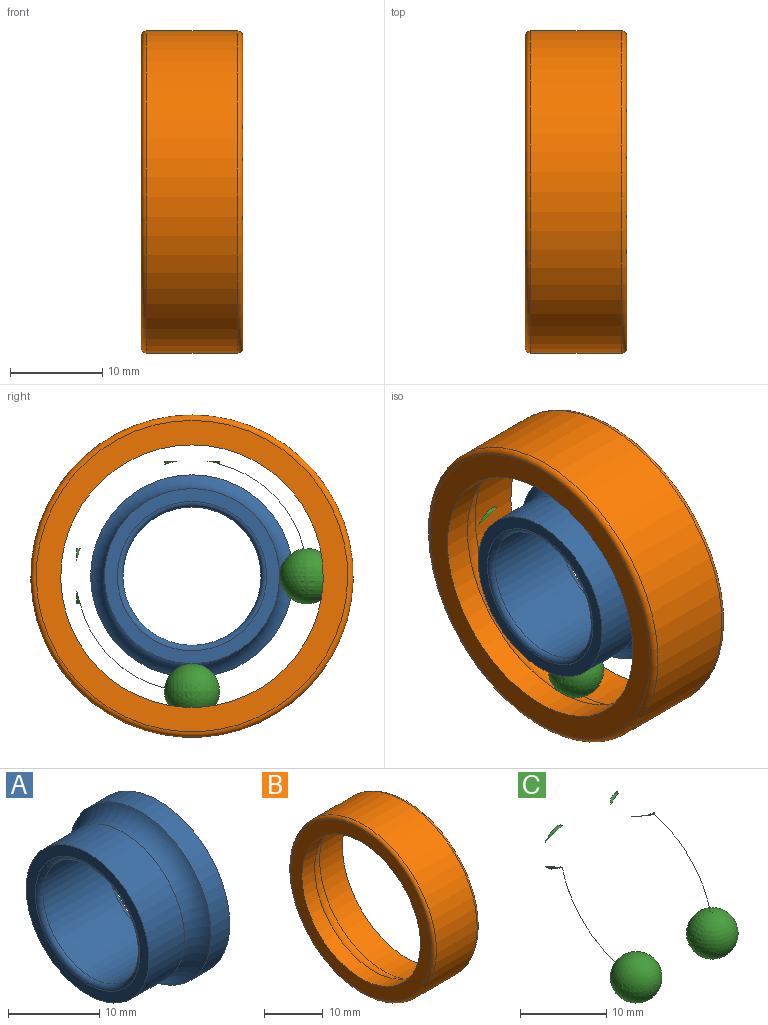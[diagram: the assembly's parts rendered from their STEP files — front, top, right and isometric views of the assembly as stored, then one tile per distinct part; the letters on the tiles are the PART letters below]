
ASSEMBLY  parts=3 mates=3
PART A: 8 faces, bbox 11x27.1x27.1 mm
  f0: torus R=8.1mm, axis (-1,0,0), area 45.7mm2, adj f1,f7
  f1: cylinder r=7.5mm len=15mm, axis (-1,0,0), area 461.8mm2, adj f0,f2
  f2: torus R=8.1mm, axis (-1,0,0), area 45.7mm2, adj f1,f3
  f3: plane 22x22mm, normal (1,0,0), area 174mm2, adj f2,f4
  f4: cylinder r=11mm len=22mm, axis (-1,0,0), area 199.8mm2, adj f3,f5
  f5: torus R=12.5mm, axis (-1,0,0), area 197.8mm2, adj f4,f6
  f6: cylinder r=9.5mm len=19mm, axis (-1,0,0), area 329mm2, adj f5,f7
  f7: plane 19x19mm, normal (-1,0,0), area 77.4mm2, adj f0,f6
PART B: 8 faces, bbox 11x37.9x37.9 mm
  f0: cylinder r=14.25mm len=28.5mm, axis (-1,0,0), area 275.3mm2, adj f1,f7
  f1: torus R=12.5mm, axis (-1,0,0), area 269.3mm2, adj f0,f2
  f2: cylinder r=15.5mm len=31mm, axis (-1,0,0), area 534.5mm2, adj f1,f3
  f3: plane 33.8x33.8mm, normal (1,0,0), area 142.5mm2, adj f2,f4
  f4: torus R=16.9mm, axis (-1,0,0), area 102.3mm2, adj f3,f5
  f5: cylinder r=17.5mm len=35mm, axis (-1,0,0), area 1077.6mm2, adj f4,f6
  f6: torus R=16.9mm, axis (-1,0,0), area 102.3mm2, adj f5,f7
  f7: plane 33.8x33.8mm, normal (-1,0,0), area 259.3mm2, adj f0,f6
PART C: 8 faces, bbox 6x31x31 mm
  f0: torus R=12.5mm, axis (1,0,0), area 0.1mm2, adj f6,f7
  f1: torus R=12.5mm, axis (1,0,0), area 0.1mm2, adj f4,f7
  f2: torus R=12.5mm, axis (1,0,0), area 0.1mm2, adj f5,f6
  f3: torus R=12.5mm, axis (1,0,0), area 0.1mm2, adj f4,f5
  f4: sphere r=3mm, area 113.1mm2, adj f1,f3
  f5: sphere r=3mm, area 113.1mm2, adj f2,f3
  f6: sphere r=3mm, area 113.1mm2, adj f0,f2
  f7: sphere r=3mm, area 113.1mm2, adj f0,f1
PLACE A t=(-2.76,0,0)mm
PLACE B t=(-2.76,0,0)mm
PLACE C t=(-2.76,0,0)mm
MATE planar B.f0 <-> A.f0  axis (1,0,0) through (8.24,0,0)mm
MATE cylindrical C.f0 <-> A.f0  axis (1,0,0) through (2.74,0,0)mm
MATE cylindrical B.f0 <-> A.f0  axis (-1,0,0) through (5.5,0,0)mm
